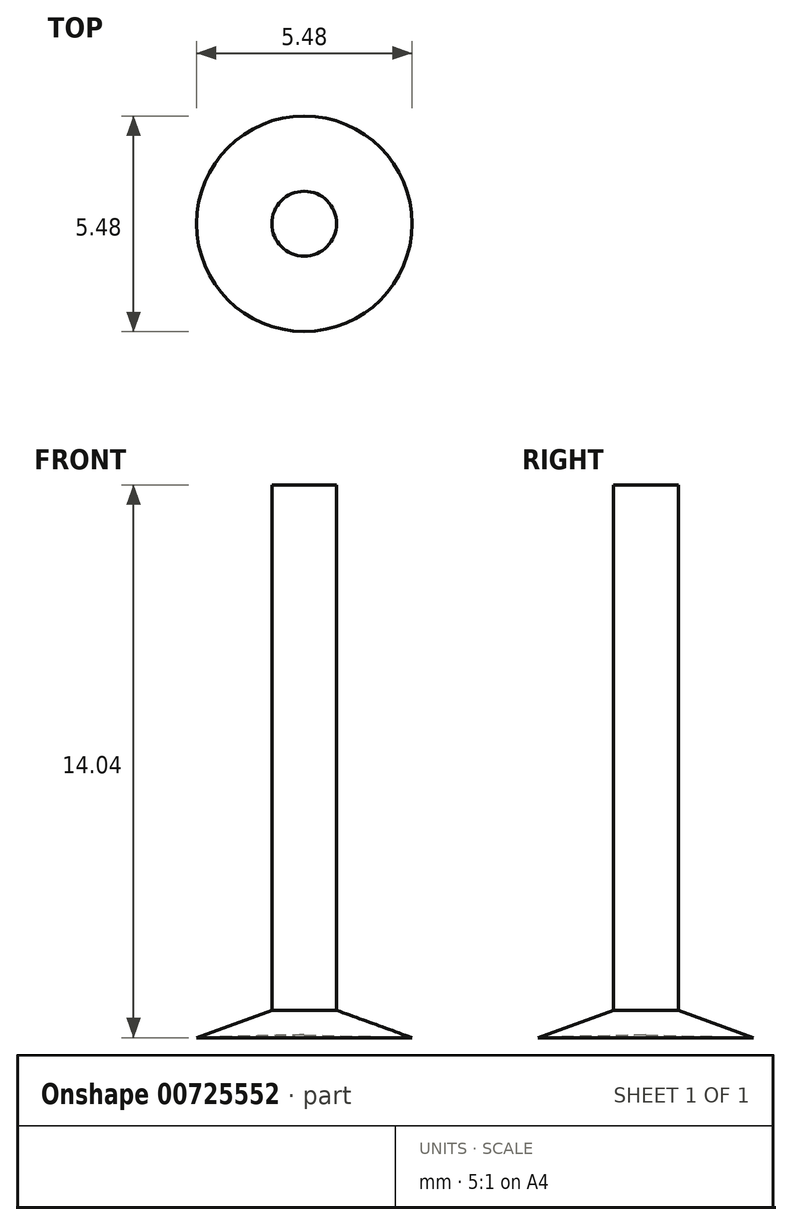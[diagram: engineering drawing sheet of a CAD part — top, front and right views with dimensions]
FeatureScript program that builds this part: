
annotation { "Feature Type Name" : "Feature", "Feature Type Description" : "" }
export const myFeature = defineFeature(function(context is Context, id is Id, definition is map)
    precondition{}
    {
        {
            var Q0;
            Q0=qCreatedBy(makeId("Front.planeOp"),FACE);
            var sketch = newSketch(context, id + "F0", { "sketchPlane" : qUnion([Q0])});
            skLineSegment(sketch, "E0", {"start": v(-2.3, -3.66) * mm, "end": v(-0.38, -2.96) * mm});
            skLineSegment(sketch, "E1", {"start": v(-2.3, -3.66) * mm, "end": v(0.44, -3.59) * mm});
            skLineSegment(sketch, "E2", {"start": v(0.44, -3.59) * mm, "end": v(0.44, 10.38) * mm});
            skLineSegment(sketch, "E3", {"start": v(-0.38, -2.96) * mm, "end": v(-0.38, 10.38) * mm});
            skLineSegment(sketch, "E4", {"start": v(-0.38, 10.38) * mm, "end": v(0.44, 10.38) * mm});
            skLineSegment(sketch, "E5", {"start": v(0.44, 11.06) * mm, "end": v(0.44, -4.32) * mm, "construction": true});
            skSolve(sketch);
        }
        {
            var Q0;
            Q0 = qSketchRegion(id + "F0", true);
            var Q1;
            Q1=sQuery(id+"F0.wireOp",EDGE,"E5");
            revolve(context, id + "F1", {"surfaceOperationType" : NewSurfaceOperationType.NEW, "entities" : qUnion([Q0]), "axis" : qUnion([Q1]), "revolveType" : RevolveType.FULL});
        }
    });
